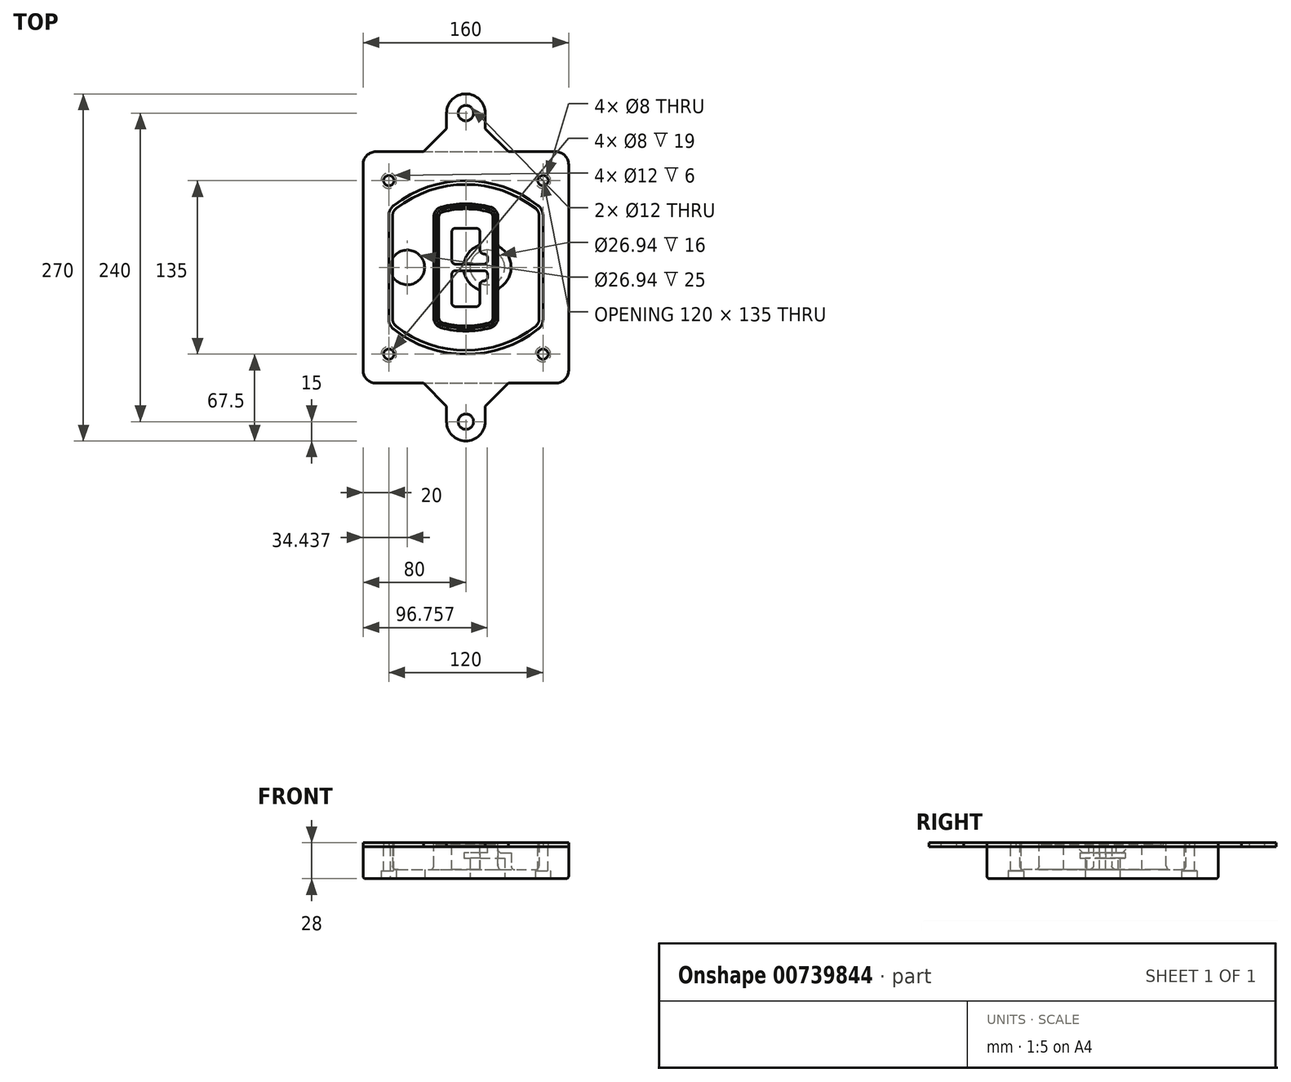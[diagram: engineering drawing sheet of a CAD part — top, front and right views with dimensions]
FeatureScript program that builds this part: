
annotation { "Feature Type Name" : "Feature", "Feature Type Description" : "" }
export const myFeature = defineFeature(function(context is Context, id is Id, definition is map)
    precondition{}
    {
        {
            var Q0;
            Q0=qCreatedBy(makeId("Top.planeOp"),FACE);
            var sketch = newSketch(context, id + "F0", { "sketchPlane" : qUnion([Q0])});
            skPoint(sketch, "E0.rect.middle", {"position": v(0, 0) * mm});
            skLineSegment(sketch, "E1.bottom", {"start": v(-70, -90) * mm, "end": v(70, -90) * mm});
            skLineSegment(sketch, "E1.top", {"start": v(-70, 90) * mm, "end": v(70, 90) * mm});
            skLineSegment(sketch, "E1.left", {"start": v(-80, -80) * mm, "end": v(-80, 80) * mm});
            skLineSegment(sketch, "E1.right", {"start": v(80, -80) * mm, "end": v(80, 80) * mm});
            skLineSegment(sketch, "E2", {"start": v(-80, 90) * mm, "end": v(80, -90) * mm, "construction": true});
            skLineSegment(sketch, "E3", {"start": v(80, 90) * mm, "end": v(-80, -90) * mm, "construction": true});
            skCircle(sketch, "E4", {"center": v(-60, 67.5) * mm, "radius": 4 * mm});
            skCircle(sketch, "E5", {"center": v(60, 67.5) * mm, "radius": 4 * mm});
            skCircle(sketch, "E6", {"center": v(60, -67.5) * mm, "radius": 4 * mm});
            skCircle(sketch, "E7", {"center": v(-60, -67.5) * mm, "radius": 4 * mm});
            skLineSegment(sketch, "E8", {"start": v(-60, 67.5) * mm, "end": v(60, 67.5) * mm, "construction": true});
            skLineSegment(sketch, "E9", {"start": v(60, 67.5) * mm, "end": v(60, -67.5) * mm, "construction": true});
            skLineSegment(sketch, "E10", {"start": v(60, -67.5) * mm, "end": v(-60, -67.5) * mm, "construction": true});
            skLineSegment(sketch, "E11", {"start": v(-60, -67.5) * mm, "end": v(-60, 67.5) * mm, "construction": true});
            skLineSegment(sketch, "E12", {"start": v(-60, 40.3) * mm, "end": v(-60, -40.3) * mm});
            skLineSegment(sketch, "E13", {"start": v(60, 40.3) * mm, "end": v(60, -40.3) * mm});
            skArc(sketch, "E14", {"start": v(56.15, 48.18) * mm, "mid": v(0, 67.5) * mm, "end": v(-56.15, 48.18) * mm});
            skArc(sketch, "E15", {"start": v(-56.15, -48.18) * mm, "mid": v(0, -67.5) * mm, "end": v(56.15, -48.18) * mm});
            skLineSegment(sketch, "E16", {"start": v(-60, 0) * mm, "end": v(60, 0) * mm, "construction": true});
            skPoint(sketch, "E17.visualSharp", {"position": v(-60, -45) * mm});
            skArc(sketch, "E17.filletArc", {"start": v(-60, -40.3) * mm, "mid": v(-58.99, -44.68) * mm, "end": v(-56.15, -48.18) * mm});
            skPoint(sketch, "E18.visualSharp", {"position": v(-60, 45) * mm});
            skArc(sketch, "E18.filletArc", {"start": v(-56.15, 48.18) * mm, "mid": v(-58.99, 44.68) * mm, "end": v(-60, 40.3) * mm});
            skPoint(sketch, "E19.visualSharp", {"position": v(60, 45) * mm});
            skArc(sketch, "E19.filletArc", {"start": v(60, 40.3) * mm, "mid": v(58.99, 44.68) * mm, "end": v(56.15, 48.18) * mm});
            skPoint(sketch, "E20.visualSharp", {"position": v(60, -45) * mm});
            skArc(sketch, "E20.filletArc", {"start": v(56.15, -48.18) * mm, "mid": v(58.99, -44.68) * mm, "end": v(60, -40.3) * mm});
            skPoint(sketch, "E21.visualSharp", {"position": v(-80, 90) * mm});
            skArc(sketch, "E21.filletArc", {"start": v(-70, 90) * mm, "mid": v(-77.07, 87.07) * mm, "end": v(-80, 80) * mm});
            skPoint(sketch, "E22.visualSharp", {"position": v(80, 90) * mm});
            skArc(sketch, "E22.filletArc", {"start": v(80, 80) * mm, "mid": v(77.07, 87.07) * mm, "end": v(70, 90) * mm});
            skPoint(sketch, "E23.visualSharp", {"position": v(80, -90) * mm});
            skArc(sketch, "E23.filletArc", {"start": v(70, -90) * mm, "mid": v(77.07, -87.07) * mm, "end": v(80, -80) * mm});
            skPoint(sketch, "E24.visualSharp", {"position": v(-80, -90) * mm});
            skArc(sketch, "E24.filletArc", {"start": v(-80, -80) * mm, "mid": v(-77.07, -87.07) * mm, "end": v(-70, -90) * mm});
            skArc(sketch, "E25.0", {"start": v(57, 40.3) * mm, "mid": v(56.3, 43.36) * mm, "end": v(54.3, 45.81) * mm});
            skLineSegment(sketch, "E25.1", {"start": v(57, 40.3) * mm, "end": v(57, -40.3) * mm});
            skArc(sketch, "E25.2", {"start": v(54.3, -45.81) * mm, "mid": v(56.3, -43.36) * mm, "end": v(57, -40.3) * mm});
            skArc(sketch, "E25.3", {"start": v(-54.3, -45.81) * mm, "mid": v(0, -64.5) * mm, "end": v(54.3, -45.81) * mm});
            skArc(sketch, "E25.4", {"start": v(-57, -40.3) * mm, "mid": v(-56.3, -43.36) * mm, "end": v(-54.3, -45.81) * mm});
            skArc(sketch, "E25.5", {"start": v(54.3, 45.81) * mm, "mid": v(0, 64.5) * mm, "end": v(-54.3, 45.81) * mm});
            skLineSegment(sketch, "E25.6", {"start": v(-57, 40.3) * mm, "end": v(-57, -40.3) * mm});
            skArc(sketch, "E25.7", {"start": v(-54.3, 45.81) * mm, "mid": v(-56.3, 43.36) * mm, "end": v(-57, 40.3) * mm});
            skArc(sketch, "E26.0", {"start": v(-58.62, 51.33) * mm, "mid": v(-62.58, 46.43) * mm, "end": v(-64, 40.3) * mm});
            skArc(sketch, "E26.1", {"start": v(58.62, 51.33) * mm, "mid": v(0, 71.5) * mm, "end": v(-58.62, 51.33) * mm});
            skArc(sketch, "E26.2", {"start": v(64, 40.3) * mm, "mid": v(62.58, 46.43) * mm, "end": v(58.62, 51.33) * mm});
            skLineSegment(sketch, "E26.3", {"start": v(64, 40.3) * mm, "end": v(64, -40.3) * mm});
            skArc(sketch, "E26.4", {"start": v(58.62, -51.33) * mm, "mid": v(62.58, -46.43) * mm, "end": v(64, -40.3) * mm});
            skLineSegment(sketch, "E26.5", {"start": v(-64, 40.3) * mm, "end": v(-64, -40.3) * mm});
            skArc(sketch, "E26.6", {"start": v(-58.62, -51.33) * mm, "mid": v(0, -71.5) * mm, "end": v(58.62, -51.33) * mm});
            skArc(sketch, "E26.7", {"start": v(-64, -40.3) * mm, "mid": v(-62.58, -46.43) * mm, "end": v(-58.62, -51.33) * mm});
            skSolve(sketch);
        }
        {
            var Q0;
            Q0=makeQuery(id+"F0.imprint","IMPRINT",FACE,{"disambiguationData":[TD([[makeQuery(id+"F0.imprint","IMPRINT",EDGE,{"derivedFrom":sQuery(id+"F0.wireOp",EDGE,"E1.bottom")}),1.0]])]});
            var Q1;
            Q1=makeQuery(id+"F0.imprint","IMPRINT",FACE,{"disambiguationData":[TD([[makeQuery(id+"F0.imprint","IMPRINT",EDGE,{"derivedFrom":sQuery(id+"F0.wireOp",EDGE,"E12")}),1.0]])]});
            var Q2;
            Q2=makeQuery(id+"F0.imprint","IMPRINT",FACE,{"disambiguationData":[TD([[makeQuery(id+"F0.imprint","IMPRINT",EDGE,{"derivedFrom":sQuery(id+"F0.wireOp",EDGE,"E25.0")}),1.0]])]});
            var Q3;
            Q3=makeQuery(id+"F0.imprint","IMPRINT",FACE,{"disambiguationData":[TD([[makeQuery(id+"F0.imprint","IMPRINT",EDGE,{"derivedFrom":sQuery(id+"F0.wireOp",EDGE,"E12")}),-1.0]])]});
            extrude(context, id + "F1", {"entities" : qUnion([Q0, Q1, Q2, Q3]), "oppositeDirection" : true, "depth" : 25 * mm});
        }
        {
            var Q0;
            Q0=makeQuery(id+"F0.imprint","IMPRINT",FACE,{"disambiguationData":[TD([[makeQuery(id+"F0.imprint","IMPRINT",EDGE,{"derivedFrom":sQuery(id+"F0.wireOp",EDGE,"E12")}),1.0]])]});
            extrude(context, id + "F2", {"entities" : qUnion([Q0]), "operationType" : NewBodyOperationType.ADD, "depth" : 3 * mm});
        }
        {
            var Q0;
            Q0=makeQuery(id+"F0.imprint","IMPRINT",FACE,{"disambiguationData":[TD([[makeQuery(id+"F0.imprint","IMPRINT",EDGE,{"derivedFrom":sQuery(id+"F0.wireOp",EDGE,"E25.0")}),1.0]])]});
            extrude(context, id + "F3", {"entities" : qUnion([Q0]), "operationType" : NewBodyOperationType.REMOVE, "oppositeDirection" : true, "depth" : 18 * mm});
        }
        {
            var Q0;
            Q0=makeQuery(id+"F2.opExtrude","CAP_FACE",FACE,{"disambiguationData":[OSD([sQuery(id+"F0.wireOp",EDGE,"E12"),sQuery(id+"F0.wireOp",EDGE,"E13"),sQuery(id+"F0.wireOp",EDGE,"E14"),sQuery(id+"F0.wireOp",EDGE,"E15"),sQuery(id+"F0.wireOp",EDGE,"E17.filletArc"),sQuery(id+"F0.wireOp",EDGE,"E18.filletArc"),sQuery(id+"F0.wireOp",EDGE,"E19.filletArc"),sQuery(id+"F0.wireOp",EDGE,"E20.filletArc"),sQuery(id+"F0.wireOp",EDGE,"E25.0"),sQuery(id+"F0.wireOp",EDGE,"E25.1"),sQuery(id+"F0.wireOp",EDGE,"E25.2"),sQuery(id+"F0.wireOp",EDGE,"E25.3"),sQuery(id+"F0.wireOp",EDGE,"E25.4"),sQuery(id+"F0.wireOp",EDGE,"E25.5"),sQuery(id+"F0.wireOp",EDGE,"E25.6"),sQuery(id+"F0.wireOp",EDGE,"E25.7")])],"isStart":false});
            var sketch = newSketch(context, id + "F4", { "sketchPlane" : qUnion([Q0])});
            skArc(sketch, "E27.0", {"start": v(-19.08, -46.97) * mm, "mid": v(0, -49.5) * mm, "end": v(19.08, -46.97) * mm});
            skArc(sketch, "E28.0", {"start": v(19.08, 46.97) * mm, "mid": v(0, 49.5) * mm, "end": v(-19.08, 46.97) * mm});
            skLineSegment(sketch, "E29", {"start": v(-25, 39.25) * mm, "end": v(-25, -39.25) * mm});
            skLineSegment(sketch, "E30", {"start": v(25, 39.25) * mm, "end": v(25, -39.25) * mm});
            skLineSegment(sketch, "E31", {"start": v(-25, 45.1) * mm, "end": v(25, 45.1) * mm, "construction": true});
            skLineSegment(sketch, "E32", {"start": v(-25, -45.1) * mm, "end": v(25, -45.1) * mm, "construction": true});
            skPoint(sketch, "E33.visualSharp", {"position": v(-25, 45.1) * mm});
            skArc(sketch, "E33.filletArc", {"start": v(-19.08, 46.97) * mm, "mid": v(-23.35, 44.11) * mm, "end": v(-25, 39.25) * mm});
            skPoint(sketch, "E34.visualSharp", {"position": v(25, 45.1) * mm});
            skArc(sketch, "E34.filletArc", {"start": v(25, 39.25) * mm, "mid": v(23.35, 44.11) * mm, "end": v(19.08, 46.97) * mm});
            skPoint(sketch, "E35.visualSharp", {"position": v(25, -45.1) * mm});
            skArc(sketch, "E35.filletArc", {"start": v(19.08, -46.97) * mm, "mid": v(23.35, -44.11) * mm, "end": v(25, -39.25) * mm});
            skPoint(sketch, "E36.visualSharp", {"position": v(-25, -45.1) * mm});
            skArc(sketch, "E36.filletArc", {"start": v(-25, -39.25) * mm, "mid": v(-23.35, -44.11) * mm, "end": v(-19.08, -46.97) * mm});
            skArc(sketch, "E37.0", {"start": v(54.3, 45.81) * mm, "mid": v(0, 64.5) * mm, "end": v(-54.3, 45.81) * mm});
            skArc(sketch, "E37.1", {"start": v(-54.3, 45.81) * mm, "mid": v(-56.3, 43.36) * mm, "end": v(-57, 40.3) * mm});
            skLineSegment(sketch, "E37.2", {"start": v(-57, 40.3) * mm, "end": v(-57, -40.3) * mm});
            skArc(sketch, "E37.3", {"start": v(-57, -40.3) * mm, "mid": v(-56.3, -43.36) * mm, "end": v(-54.3, -45.81) * mm});
            skArc(sketch, "E37.4", {"start": v(-54.3, -45.81) * mm, "mid": v(0, -64.5) * mm, "end": v(54.3, -45.81) * mm});
            skArc(sketch, "E37.5", {"start": v(54.3, -45.81) * mm, "mid": v(56.3, -43.36) * mm, "end": v(57, -40.3) * mm});
            skLineSegment(sketch, "E37.6", {"start": v(57, 40.3) * mm, "end": v(57, -40.3) * mm});
            skArc(sketch, "E37.7", {"start": v(57, 40.3) * mm, "mid": v(56.3, 43.36) * mm, "end": v(54.3, 45.81) * mm});
            skLineSegment(sketch, "E38.0", {"start": v(23, 39.25) * mm, "end": v(23, -39.25) * mm});
            skArc(sketch, "E38.1", {"start": v(18.56, -45.04) * mm, "mid": v(21.76, -42.9) * mm, "end": v(23, -39.25) * mm});
            skArc(sketch, "E38.2", {"start": v(-18.56, -45.04) * mm, "mid": v(0, -47.5) * mm, "end": v(18.56, -45.04) * mm});
            skArc(sketch, "E38.3", {"start": v(-23, -39.25) * mm, "mid": v(-21.76, -42.9) * mm, "end": v(-18.56, -45.04) * mm});
            skLineSegment(sketch, "E38.4", {"start": v(-23, 39.25) * mm, "end": v(-23, -39.25) * mm});
            skArc(sketch, "E38.5", {"start": v(23, 39.25) * mm, "mid": v(21.76, 42.9) * mm, "end": v(18.56, 45.04) * mm});
            skArc(sketch, "E38.6", {"start": v(-18.56, 45.04) * mm, "mid": v(-21.76, 42.9) * mm, "end": v(-23, 39.25) * mm});
            skArc(sketch, "E38.7", {"start": v(18.56, 45.04) * mm, "mid": v(0, 47.5) * mm, "end": v(-18.56, 45.04) * mm});
            skArc(sketch, "E39.0", {"start": v(21, 39.25) * mm, "mid": v(20.18, 41.68) * mm, "end": v(18.04, 43.1) * mm});
            skLineSegment(sketch, "E39.1", {"start": v(21, 39.25) * mm, "end": v(21, -39.25) * mm});
            skArc(sketch, "E39.2", {"start": v(18.04, -43.1) * mm, "mid": v(20.18, -41.68) * mm, "end": v(21, -39.25) * mm});
            skArc(sketch, "E39.3", {"start": v(-18.04, -43.1) * mm, "mid": v(0, -45.5) * mm, "end": v(18.04, -43.1) * mm});
            skArc(sketch, "E39.4", {"start": v(-21, -39.25) * mm, "mid": v(-20.18, -41.68) * mm, "end": v(-18.04, -43.1) * mm});
            skArc(sketch, "E39.5", {"start": v(18.04, 43.1) * mm, "mid": v(0, 45.5) * mm, "end": v(-18.04, 43.1) * mm});
            skLineSegment(sketch, "E39.6", {"start": v(-21, 39.25) * mm, "end": v(-21, -39.25) * mm});
            skArc(sketch, "E39.7", {"start": v(-18.04, 43.1) * mm, "mid": v(-20.18, 41.68) * mm, "end": v(-21, 39.25) * mm});
            skLineSegment(sketch, "E40", {"start": v(-25, 0) * mm, "end": v(25, 0) * mm, "construction": true});
            skLineSegment(sketch, "E41", {"start": v(-11, 5.5) * mm, "end": v(-11, 27.5) * mm});
            skLineSegment(sketch, "E42", {"start": v(-8, 30.5) * mm, "end": v(8, 30.5) * mm});
            skLineSegment(sketch, "E43", {"start": v(11, 27.5) * mm, "end": v(11, 13.5) * mm});
            skLineSegment(sketch, "E44", {"start": v(14, 10.5) * mm, "end": v(14, 10.5) * mm});
            skLineSegment(sketch, "E45", {"start": v(17, 7.5) * mm, "end": v(17, 5.5) * mm});
            skLineSegment(sketch, "E46", {"start": v(14, 2.5) * mm, "end": v(-8, 2.5) * mm});
            skPoint(sketch, "E47.visualSharp", {"position": v(-11, 30.5) * mm});
            skArc(sketch, "E47.filletArc", {"start": v(-8, 30.5) * mm, "mid": v(-10.12, 29.62) * mm, "end": v(-11, 27.5) * mm});
            skPoint(sketch, "E48.visualSharp", {"position": v(11, 30.5) * mm});
            skArc(sketch, "E48.filletArc", {"start": v(11, 27.5) * mm, "mid": v(10.12, 29.62) * mm, "end": v(8, 30.5) * mm});
            skPoint(sketch, "E49.visualSharp", {"position": v(11, 10.5) * mm});
            skArc(sketch, "E49.filletArc", {"start": v(11, 13.5) * mm, "mid": v(11.88, 11.38) * mm, "end": v(14, 10.5) * mm});
            skPoint(sketch, "E50.visualSharp", {"position": v(17, 10.5) * mm});
            skArc(sketch, "E50.filletArc", {"start": v(17, 7.5) * mm, "mid": v(16.12, 9.62) * mm, "end": v(14, 10.5) * mm});
            skPoint(sketch, "E51.visualSharp", {"position": v(17, 2.5) * mm});
            skArc(sketch, "E51.filletArc", {"start": v(14, 2.5) * mm, "mid": v(16.12, 3.38) * mm, "end": v(17, 5.5) * mm});
            skPoint(sketch, "E52.visualSharp", {"position": v(-11, 2.5) * mm});
            skArc(sketch, "E52.filletArc", {"start": v(-11, 5.5) * mm, "mid": v(-10.12, 3.38) * mm, "end": v(-8, 2.5) * mm});
            skLineSegment(sketch, "E53.0.MirrorCS", {"start": v(14, -2.5) * mm, "end": v(-8, -2.5) * mm});
            skArc(sketch, "E54.0.MirrorCS", {"start": v(-11, -5.5) * mm, "mid": v(-10.12, -3.38) * mm, "end": v(-8, -2.5) * mm});
            skLineSegment(sketch, "E55.0.MirrorCS", {"start": v(-11, -5.5) * mm, "end": v(-11, -27.5) * mm});
            skArc(sketch, "E56.0.MirrorCS", {"start": v(-8, -30.5) * mm, "mid": v(-10.12, -29.62) * mm, "end": v(-11, -27.5) * mm});
            skLineSegment(sketch, "E57.0.MirrorCS", {"start": v(-8, -30.5) * mm, "end": v(8, -30.5) * mm});
            skArc(sketch, "E58.0.MirrorCS", {"start": v(11, -27.5) * mm, "mid": v(10.12, -29.62) * mm, "end": v(8, -30.5) * mm});
            skLineSegment(sketch, "E59.0.MirrorCS", {"start": v(11, -27.5) * mm, "end": v(11, -13.5) * mm});
            skArc(sketch, "E60.0.MirrorCS", {"start": v(11, -13.5) * mm, "mid": v(11.88, -11.38) * mm, "end": v(14, -10.5) * mm});
            skArc(sketch, "E61.0.MirrorCS", {"start": v(17, -7.5) * mm, "mid": v(16.12, -9.62) * mm, "end": v(14, -10.5) * mm});
            skLineSegment(sketch, "E62.0.MirrorCS", {"start": v(17, -7.5) * mm, "end": v(17, -5.5) * mm});
            skArc(sketch, "E63.0.MirrorCS", {"start": v(14, -2.5) * mm, "mid": v(16.12, -3.38) * mm, "end": v(17, -5.5) * mm});
            skSolve(sketch);
        }
        {
            var Q0;
            Q0=makeQuery(id+"F4.imprint","IMPRINT",FACE,{"disambiguationData":[TD([[makeQuery(id+"F4.imprint","IMPRINT",EDGE,{"derivedFrom":sQuery(id+"F4.wireOp",EDGE,"E27.0")}),1.0]])]});
            var Q1;
            Q1=makeQuery(id+"F4.imprint","IMPRINT",FACE,{"disambiguationData":[TD([[makeQuery(id+"F4.imprint","IMPRINT",EDGE,{"derivedFrom":sQuery(id+"F4.wireOp",EDGE,"E38.0")}),-1.0]])]});
            var Q2;
            Q2=makeQuery(id+"F4.imprint","IMPRINT",FACE,{"disambiguationData":[TD([[makeQuery(id+"F4.imprint","IMPRINT",EDGE,{"derivedFrom":sQuery(id+"F4.wireOp",EDGE,"E39.0")}),1.0]])]});
            extrude(context, id + "F5", {"entities" : qUnion([Q0, Q1, Q2]), "operationType" : NewBodyOperationType.ADD, "endBound" : BoundingType.UP_TO_NEXT, "oppositeDirection" : true, "depth" : 25 * mm});
        }
        {
            var Q0;
            Q0=makeQuery(id+"F4.imprint","IMPRINT",FACE,{"disambiguationData":[TD([[makeQuery(id+"F4.imprint","IMPRINT",EDGE,{"derivedFrom":sQuery(id+"F4.wireOp",EDGE,"E38.0")}),-1.0]])]});
            extrude(context, id + "F6", {"entities" : qUnion([Q0]), "operationType" : NewBodyOperationType.REMOVE, "oppositeDirection" : true, "depth" : 2 * mm});
        }
        {
            var Q0;
            Q0=makeQuery(id+"F1.opExtrude","CAP_FACE",FACE,{"disambiguationData":[OSD([sQuery(id+"F0.wireOp",EDGE,"E1.bottom"),sQuery(id+"F0.wireOp",EDGE,"E1.top"),sQuery(id+"F0.wireOp",EDGE,"E1.left"),sQuery(id+"F0.wireOp",EDGE,"E1.right"),sQuery(id+"F0.wireOp",EDGE,"E4"),sQuery(id+"F0.wireOp",EDGE,"E5"),sQuery(id+"F0.wireOp",EDGE,"E6"),sQuery(id+"F0.wireOp",EDGE,"E7"),sQuery(id+"F0.wireOp",EDGE,"E21.filletArc"),sQuery(id+"F0.wireOp",EDGE,"E22.filletArc"),sQuery(id+"F0.wireOp",EDGE,"E23.filletArc"),sQuery(id+"F0.wireOp",EDGE,"E24.filletArc")])],"isStart":false});
            var sketch = newSketch(context, id + "F7", { "sketchPlane" : qUnion([Q0])});
            skCircle(sketch, "E64", {"center": v(16.76, 0) * mm, "radius": 13.47 * mm});
            skCircle(sketch, "E65", {"center": v(-45.56, 0) * mm, "radius": 13.47 * mm});
            skLineSegment(sketch, "E66", {"start": v(80, 0) * mm, "end": v(-80, 0) * mm});
            skCircle(sketch, "E67", {"center": v(16.76, 0) * mm, "radius": 18.47 * mm});
            skCircle(sketch, "E68", {"center": v(60, -67.5) * mm, "radius": 6 * mm});
            skCircle(sketch, "E69", {"center": v(-60, -67.5) * mm, "radius": 6 * mm});
            skCircle(sketch, "E70", {"center": v(-60, 67.5) * mm, "radius": 6 * mm});
            skCircle(sketch, "E71", {"center": v(60, 67.5) * mm, "radius": 6 * mm});
            skSolve(sketch);
        }
        {
            var Q0;
            {var subQ1=sQuery(id+"F7.wireOp",EDGE,"E66");var subQ4=sQuery(id+"F7.wireOp",EDGE,"E64");var subQ6=makeQuery(id+"F7.imprint","INTERSECT",VERTEX,{"disambiguationData":[OD(0.0)],"derivedFrom":[subQ4,subQ1]});Q0=makeQuery(id+"F7.imprint","IMPRINT",FACE,{"disambiguationData":[TD([[makeQuery(id+"F7.imprint","IMPRINT",EDGE,{"disambiguationData":[TD([[subQ6,-1.0]])],"derivedFrom":subQ4}),-1.0]])]});}
            var Q1;
            {var subQ0=sQuery(id+"F7.wireOp",EDGE,"E66");var subQ1=sQuery(id+"F7.wireOp",EDGE,"E64");var subQ3=makeQuery(id+"F7.imprint","INTERSECT",VERTEX,{"disambiguationData":[OD(0.0)],"derivedFrom":[subQ1,subQ0]});Q1=makeQuery(id+"F7.imprint","IMPRINT",FACE,{"disambiguationData":[TD([[makeQuery(id+"F7.imprint","IMPRINT",EDGE,{"disambiguationData":[TD([[subQ3,-1.0]])],"derivedFrom":subQ1}),1.0]])]});}
            var Q2;
            {var subQ0=sQuery(id+"F7.wireOp",EDGE,"E66");var subQ1=sQuery(id+"F7.wireOp",EDGE,"E64");var subQ3=makeQuery(id+"F7.imprint","INTERSECT",VERTEX,{"disambiguationData":[OD(0.0)],"derivedFrom":[subQ1,subQ0]});Q2=makeQuery(id+"F7.imprint","IMPRINT",FACE,{"disambiguationData":[TD([[makeQuery(id+"F7.imprint","IMPRINT",EDGE,{"disambiguationData":[TD([[subQ3,1.0]])],"derivedFrom":subQ1}),1.0]])]});}
            var Q3;
            {var subQ1=sQuery(id+"F7.wireOp",EDGE,"E66");var subQ4=sQuery(id+"F7.wireOp",EDGE,"E64");var subQ6=makeQuery(id+"F7.imprint","INTERSECT",VERTEX,{"disambiguationData":[OD(0.0)],"derivedFrom":[subQ4,subQ1]});Q3=makeQuery(id+"F7.imprint","IMPRINT",FACE,{"disambiguationData":[TD([[makeQuery(id+"F7.imprint","IMPRINT",EDGE,{"disambiguationData":[TD([[subQ6,1.0]])],"derivedFrom":subQ4}),-1.0]])]});}
            extrude(context, id + "F8", {"entities" : qUnion([Q0, Q1, Q2, Q3]), "operationType" : NewBodyOperationType.ADD, "oppositeDirection" : true, "depth" : 20 * mm});
        }
        {
            var Q0;
            {var subQ0=sQuery(id+"F7.wireOp",EDGE,"E66");var subQ1=sQuery(id+"F7.wireOp",EDGE,"E64");var subQ3=makeQuery(id+"F7.imprint","INTERSECT",VERTEX,{"disambiguationData":[OD(0.0)],"derivedFrom":[subQ1,subQ0]});Q0=makeQuery(id+"F7.imprint","IMPRINT",FACE,{"disambiguationData":[TD([[makeQuery(id+"F7.imprint","IMPRINT",EDGE,{"disambiguationData":[TD([[subQ3,-1.0]])],"derivedFrom":subQ1}),1.0]])]});}
            var Q1;
            {var subQ0=sQuery(id+"F7.wireOp",EDGE,"E66");var subQ1=sQuery(id+"F7.wireOp",EDGE,"E64");var subQ3=makeQuery(id+"F7.imprint","INTERSECT",VERTEX,{"disambiguationData":[OD(0.0)],"derivedFrom":[subQ1,subQ0]});Q1=makeQuery(id+"F7.imprint","IMPRINT",FACE,{"disambiguationData":[TD([[makeQuery(id+"F7.imprint","IMPRINT",EDGE,{"disambiguationData":[TD([[subQ3,1.0]])],"derivedFrom":subQ1}),1.0]])]});}
            extrude(context, id + "F9", {"entities" : qUnion([Q0, Q1]), "operationType" : NewBodyOperationType.REMOVE, "oppositeDirection" : true, "depth" : 16 * mm});
        }
        {
            var Q0;
            {var subQ0=sQuery(id+"F7.wireOp",EDGE,"E66");var subQ1=sQuery(id+"F7.wireOp",EDGE,"E65");var subQ3=makeQuery(id+"F7.imprint","INTERSECT",VERTEX,{"disambiguationData":[OD(0.0)],"derivedFrom":[subQ1,subQ0]});Q0=makeQuery(id+"F7.imprint","IMPRINT",FACE,{"disambiguationData":[TD([[makeQuery(id+"F7.imprint","IMPRINT",EDGE,{"disambiguationData":[TD([[subQ3,-1.0]])],"derivedFrom":subQ1}),1.0]])]});}
            var Q1;
            {var subQ0=sQuery(id+"F7.wireOp",EDGE,"E66");var subQ1=sQuery(id+"F7.wireOp",EDGE,"E65");var subQ3=makeQuery(id+"F7.imprint","INTERSECT",VERTEX,{"disambiguationData":[OD(0.0)],"derivedFrom":[subQ1,subQ0]});Q1=makeQuery(id+"F7.imprint","IMPRINT",FACE,{"disambiguationData":[TD([[makeQuery(id+"F7.imprint","IMPRINT",EDGE,{"disambiguationData":[TD([[subQ3,1.0]])],"derivedFrom":subQ1}),1.0]])]});}
            extrude(context, id + "F10", {"entities" : qUnion([Q0, Q1]), "operationType" : NewBodyOperationType.REMOVE, "oppositeDirection" : true, "depth" : 25 * mm});
        }
        {
            var Q0;
            Q0=makeQuery(id+"F7.imprint","IMPRINT",FACE,{"disambiguationData":[TD([[makeQuery(id+"F7.imprint","IMPRINT",EDGE,{"derivedFrom":sQuery(id+"F7.wireOp",EDGE,"E68")}),1.0]])]});
            var Q1;
            Q1=makeQuery(id+"F7.imprint","IMPRINT",FACE,{"disambiguationData":[TD([[makeQuery(id+"F7.imprint","IMPRINT",EDGE,{"derivedFrom":makeQuery(id+"F1.opExtrude","CAP_EDGE",EDGE,{"disambiguationData":[OSD([sQuery(id+"F0.wireOp",EDGE,"E5")])],"isStart":false})}),-1.0]])]});
            var Q2;
            Q2=makeQuery(id+"F7.imprint","IMPRINT",FACE,{"disambiguationData":[TD([[makeQuery(id+"F7.imprint","IMPRINT",EDGE,{"derivedFrom":sQuery(id+"F7.wireOp",EDGE,"E69")}),1.0]])]});
            var Q3;
            Q3=makeQuery(id+"F7.imprint","IMPRINT",FACE,{"disambiguationData":[TD([[makeQuery(id+"F7.imprint","IMPRINT",EDGE,{"derivedFrom":makeQuery(id+"F1.opExtrude","CAP_EDGE",EDGE,{"disambiguationData":[OSD([sQuery(id+"F0.wireOp",EDGE,"E4")])],"isStart":false})}),-1.0]])]});
            var Q4;
            Q4=makeQuery(id+"F7.imprint","IMPRINT",FACE,{"disambiguationData":[TD([[makeQuery(id+"F7.imprint","IMPRINT",EDGE,{"derivedFrom":sQuery(id+"F7.wireOp",EDGE,"E70")}),1.0]])]});
            var Q5;
            Q5=makeQuery(id+"F7.imprint","IMPRINT",FACE,{"disambiguationData":[TD([[makeQuery(id+"F7.imprint","IMPRINT",EDGE,{"derivedFrom":makeQuery(id+"F1.opExtrude","CAP_EDGE",EDGE,{"disambiguationData":[OSD([sQuery(id+"F0.wireOp",EDGE,"E7")])],"isStart":false})}),-1.0]])]});
            var Q6;
            Q6=makeQuery(id+"F7.imprint","IMPRINT",FACE,{"disambiguationData":[TD([[makeQuery(id+"F7.imprint","IMPRINT",EDGE,{"derivedFrom":sQuery(id+"F7.wireOp",EDGE,"E71")}),1.0]])]});
            var Q7;
            Q7=makeQuery(id+"F7.imprint","IMPRINT",FACE,{"disambiguationData":[TD([[makeQuery(id+"F7.imprint","IMPRINT",EDGE,{"derivedFrom":makeQuery(id+"F1.opExtrude","CAP_EDGE",EDGE,{"disambiguationData":[OSD([sQuery(id+"F0.wireOp",EDGE,"E6")])],"isStart":false})}),-1.0]])]});
            extrude(context, id + "F11", {"entities" : qUnion([Q0, Q1, Q2, Q3, Q4, Q5, Q6, Q7]), "operationType" : NewBodyOperationType.REMOVE, "oppositeDirection" : true, "depth" : 6 * mm});
        }
        {
            var Q0;
            Q0=makeQuery(id+"F9.boolean.opBoolean","COPY",FACE,{"derivedFrom":makeQuery(id+"F9.opExtrude","CAP_FACE",FACE,{"disambiguationData":[OSD([sQuery(id+"F7.wireOp",EDGE,"E64")])],"isStart":false})});
            var sketch = newSketch(context, id + "F12", { "sketchPlane" : qUnion([Q0])});
            skArc(sketch, "E72.0", {"start": v(11, 17.55) * mm, "mid": v(2.57, 11.82) * mm, "end": v(-1.54, 2.5) * mm});
            skArc(sketch, "E72.1", {"start": v(-1.54, -2.5) * mm, "mid": v(2.57, -11.82) * mm, "end": v(11, -17.55) * mm});
            skLineSegment(sketch, "E73", {"start": v(-1.54, -2.5) * mm, "end": v(14, -2.5) * mm});
            skLineSegment(sketch, "E74.0", {"start": v(14, 2.5) * mm, "end": v(-1.54, 2.5) * mm});
            skArc(sketch, "E74.1", {"start": v(14, 2.5) * mm, "mid": v(16.12, 3.38) * mm, "end": v(17, 5.5) * mm});
            skLineSegment(sketch, "E74.2", {"start": v(17, 7.5) * mm, "end": v(17, 5.5) * mm});
            skArc(sketch, "E74.3", {"start": v(17, 7.5) * mm, "mid": v(16.12, 9.62) * mm, "end": v(14, 10.5) * mm});
            skArc(sketch, "E74.4", {"start": v(11, 13.5) * mm, "mid": v(11.88, 11.38) * mm, "end": v(14, 10.5) * mm});
            skLineSegment(sketch, "E74.5", {"start": v(11, 17.55) * mm, "end": v(11, 13.5) * mm});
            skLineSegment(sketch, "E74.7", {"start": v(14, -2.5) * mm, "end": v(-1.54, -2.5) * mm});
            skArc(sketch, "E74.8", {"start": v(14, -2.5) * mm, "mid": v(16.12, -3.38) * mm, "end": v(17, -5.5) * mm});
            skLineSegment(sketch, "E74.9", {"start": v(17, -7.5) * mm, "end": v(17, -5.5) * mm});
            skArc(sketch, "E74.10", {"start": v(17, -7.5) * mm, "mid": v(16.12, -9.62) * mm, "end": v(14, -10.5) * mm});
            skArc(sketch, "E74.11", {"start": v(11, -13.5) * mm, "mid": v(11.88, -11.38) * mm, "end": v(14, -10.5) * mm});
            skLineSegment(sketch, "E74.12", {"start": v(11, -17.55) * mm, "end": v(11, -13.5) * mm});
            skPoint(sketch, "E75.orphan", {"position": v(11, -27.5) * mm});
            skPoint(sketch, "E76.orphan", {"position": v(-8, -2.5) * mm});
            skPoint(sketch, "E77.orphan", {"position": v(-8, 2.5) * mm});
            skPoint(sketch, "E78.orphan", {"position": v(11, 27.5) * mm});
            skSolve(sketch);
        }
        {
            var Q0;
            {var subQ7=sQuery(id+"F12.wireOp",EDGE,"E72.0");var subQ14=sQuery(id+"F12.wireOp",EDGE,"E72.1");var subQ16=sQuery(id+"F12.wireOp",EDGE,"E74.1");var subQ18=sQuery(id+"F12.wireOp",EDGE,"E74.8");Q0=qUnion([makeQuery(id+"F12.imprint","IMPRINT",FACE,{"disambiguationData":[TD([[makeQuery(id+"F12.imprint","IMPRINT",EDGE,{"derivedFrom":subQ7}),1.0]])]}),makeQuery(id+"F12.imprint","IMPRINT",FACE,{"disambiguationData":[TD([[makeQuery(id+"F12.imprint","IMPRINT",EDGE,{"derivedFrom":subQ14}),1.0]])]}),makeQuery(id+"F12.imprint","IMPRINT",FACE,{"disambiguationData":[TD([[makeQuery(id+"F12.imprint","IMPRINT",EDGE,{"derivedFrom":subQ16}),1.0]])]}),makeQuery(id+"F12.imprint","IMPRINT",FACE,{"disambiguationData":[TD([[makeQuery(id+"F12.imprint","IMPRINT",EDGE,{"derivedFrom":subQ18}),-1.0]])]})]);}
            var Q1;
            Q1=makeQuery(id+"F5.boolean.opBoolean","SPLIT",FACE,{"disambiguationData":[TD([makeQuery(id+"F5.opExtrude","SWEPT_FACE",FACE,{"disambiguationData":[OSD([sQuery(id+"F4.wireOp",EDGE,"E41")])]})])],"derivedFrom":makeQuery(id+"F3.boolean.opBoolean","COPY",FACE,{"derivedFrom":makeQuery(id+"F3.opExtrude","CAP_FACE",FACE,{"disambiguationData":[OSD([sQuery(id+"F0.wireOp",EDGE,"E25.0"),sQuery(id+"F0.wireOp",EDGE,"E25.1"),sQuery(id+"F0.wireOp",EDGE,"E25.2"),sQuery(id+"F0.wireOp",EDGE,"E25.3"),sQuery(id+"F0.wireOp",EDGE,"E25.4"),sQuery(id+"F0.wireOp",EDGE,"E25.5"),sQuery(id+"F0.wireOp",EDGE,"E25.6"),sQuery(id+"F0.wireOp",EDGE,"E25.7")])],"isStart":false})})});
            extrude(context, id + "F13", {"entities" : qUnion([Q0]), "operationType" : NewBodyOperationType.REMOVE, "endBound" : BoundingType.UP_TO_SURFACE, "endBoundEntityFace" : qUnion([Q1]), "depth" : 25 * mm});
        }
        {
            var Q0;
            Q0=makeQuery(id+"F3.boolean.opBoolean","COPY",EDGE,{"derivedFrom":makeQuery(id+"F3.opExtrude","CAP_EDGE",EDGE,{"disambiguationData":[OSD([sQuery(id+"F0.wireOp",EDGE,"E25.6")])],"isStart":false})});
            var Q1;
            Q1=makeQuery(id+"F8.boolean.opBoolean","INTERSECT",EDGE,{"derivedFrom":[makeQuery(id+"F5.opExtrude","SWEPT_FACE",FACE,{"disambiguationData":[OSD([sQuery(id+"F4.wireOp",EDGE,"E30")])]}),makeQuery(id+"F8.opExtrude","CAP_FACE",FACE,{"disambiguationData":[OSD([sQuery(id+"F7.wireOp",EDGE,"E67")])],"isStart":false})]});
            var Q2;
            Q2=makeQuery(id+"F8.boolean.opBoolean","INTERSECT",EDGE,{"disambiguationData":[OD(1.0)],"derivedFrom":[makeQuery(id+"F5.opExtrude","SWEPT_FACE",FACE,{"disambiguationData":[OSD([sQuery(id+"F4.wireOp",EDGE,"E30")])]}),makeQuery(id+"F8.opExtrude","SWEPT_FACE",FACE,{"disambiguationData":[OSD([sQuery(id+"F7.wireOp",EDGE,"E67")])]})]});
            var Q3;
            {var subQ0=sQuery(id+"F4.wireOp",EDGE,"E30");Q3=makeQuery(id+"F8.boolean.opBoolean","SPLIT",EDGE,{"disambiguationData":[TD([makeQuery(id+"F5.opExtrude","SWEPT_FACE",FACE,{"disambiguationData":[OSD([sQuery(id+"F4.wireOp",EDGE,"E35.filletArc")])]})])],"derivedFrom":makeQuery(id+"F5.opExtrude","CAP_EDGE",EDGE,{"disambiguationData":[OSD([subQ0])],"isStart":false})});}
            var Q4;
            {var subQ0=sQuery(id+"F0.wireOp",EDGE,"E25.7");var subQ1=sQuery(id+"F0.wireOp",EDGE,"E25.1");var subQ2=sQuery(id+"F0.wireOp",EDGE,"E25.6");var subQ3=sQuery(id+"F0.wireOp",EDGE,"E25.5");var subQ4=sQuery(id+"F0.wireOp",EDGE,"E25.4");var subQ5=sQuery(id+"F0.wireOp",EDGE,"E25.0");var subQ6=sQuery(id+"F0.wireOp",EDGE,"E25.2");var subQ7=sQuery(id+"F0.wireOp",EDGE,"E25.3");Q4=makeQuery(id+"F8.boolean.opBoolean","INTERSECT",EDGE,{"derivedFrom":[makeQuery(id+"F5.boolean.opBoolean","SPLIT",FACE,{"disambiguationData":[TD([makeQuery(id+"F2.opExtrude","SWEPT_FACE",FACE,{"disambiguationData":[OSD([subQ5])]})])],"derivedFrom":makeQuery(id+"F3.boolean.opBoolean","COPY",FACE,{"derivedFrom":makeQuery(id+"F3.opExtrude","CAP_FACE",FACE,{"disambiguationData":[OSD([subQ5,subQ1,subQ6,subQ7,subQ4,subQ3,subQ2,subQ0])],"isStart":false})})}),makeQuery(id+"F8.opExtrude","SWEPT_FACE",FACE,{"disambiguationData":[OSD([sQuery(id+"F7.wireOp",EDGE,"E67")])]})]});}
            var Q5;
            Q5=makeQuery(id+"F8.boolean.opBoolean","INTERSECT",EDGE,{"disambiguationData":[OD(0.0)],"derivedFrom":[makeQuery(id+"F5.opExtrude","SWEPT_FACE",FACE,{"disambiguationData":[OSD([sQuery(id+"F4.wireOp",EDGE,"E30")])]}),makeQuery(id+"F8.opExtrude","SWEPT_FACE",FACE,{"disambiguationData":[OSD([sQuery(id+"F7.wireOp",EDGE,"E67")])]})]});
            fillet(context, id + "F14", {"entities" : qUnion([Q0, Q1, Q2, Q3, Q4, Q5]), "radius" : 3 * mm, "tangentPropagation" : true, "allowEdgeOverflow" : false});
        }
        {
            var Q0;
            Q0=makeQuery(id+"F1.opExtrude","CAP_EDGE",EDGE,{"disambiguationData":[OSD([sQuery(id+"F0.wireOp",EDGE,"E1.bottom")])],"isStart":false});
            fillet(context, id + "F15", {"entities" : qUnion([Q0]), "radius" : 2 * mm, "tangentPropagation" : true, "allowEdgeOverflow" : false});
        }
        {
            var Q0;
            {var subQ0=sQuery(id+"F0.wireOp",EDGE,"E21.filletArc");var subQ1=sQuery(id+"F0.wireOp",EDGE,"E7");var subQ2=sQuery(id+"F0.wireOp",EDGE,"E6");var subQ3=sQuery(id+"F0.wireOp",EDGE,"E5");var subQ4=sQuery(id+"F0.wireOp",EDGE,"E4");var subQ5=sQuery(id+"F0.wireOp",EDGE,"E22.filletArc");var subQ6=sQuery(id+"F0.wireOp",EDGE,"E1.bottom");var subQ7=sQuery(id+"F0.wireOp",EDGE,"E1.right");var subQ8=sQuery(id+"F0.wireOp",EDGE,"E1.top");var subQ9=sQuery(id+"F0.wireOp",EDGE,"E1.left");var subQ10=sQuery(id+"F0.wireOp",EDGE,"E23.filletArc");var subQ11=sQuery(id+"F0.wireOp",EDGE,"E24.filletArc");Q0=makeQuery(id+"F2.boolean.opBoolean","SPLIT",FACE,{"disambiguationData":[TD([makeQuery(id+"F1.opExtrude","SWEPT_FACE",FACE,{"disambiguationData":[OSD([subQ6])]})])],"derivedFrom":makeQuery(id+"F1.opExtrude","CAP_FACE",FACE,{"disambiguationData":[OSD([subQ6,subQ8,subQ9,subQ7,subQ4,subQ3,subQ2,subQ1,subQ0,subQ5,subQ10,subQ11])],"isStart":true})});}
            var sketch = newSketch(context, id + "F16", { "sketchPlane" : qUnion([Q0])});
            skLineSegment(sketch, "E79", {"start": v(0, 90) * mm, "end": v(0, 120) * mm, "construction": true});
            skCircle(sketch, "E80", {"center": v(0, 120) * mm, "radius": 6 * mm});
            skArc(sketch, "E81", {"start": v(15, 120) * mm, "mid": v(0, 135) * mm, "end": v(-15, 120) * mm});
            skLineSegment(sketch, "E82", {"start": v(-33, 90) * mm, "end": v(-15, 108) * mm});
            skLineSegment(sketch, "E83", {"start": v(-15, 108) * mm, "end": v(-15, 120) * mm});
            skLineSegment(sketch, "E84", {"start": v(15, 120) * mm, "end": v(15, 108) * mm});
            skLineSegment(sketch, "E85", {"start": v(15, 108) * mm, "end": v(33, 90) * mm});
            skLineSegment(sketch, "E86", {"start": v(-80, 0) * mm, "end": v(80, 0) * mm, "construction": true});
            skLineSegment(sketch, "E87.MirrorCS", {"start": v(-33, -90) * mm, "end": v(-15, -108) * mm});
            skLineSegment(sketch, "E88.MirrorCS", {"start": v(-15, -108) * mm, "end": v(-15, -120) * mm});
            skArc(sketch, "E89.MirrorCS", {"start": v(15, -120) * mm, "mid": v(0, -135) * mm, "end": v(-15, -120) * mm});
            skCircle(sketch, "E90.MirrorC", {"center": v(0, -120) * mm, "radius": 6 * mm});
            skLineSegment(sketch, "E91.MirrorCS", {"start": v(15, -120) * mm, "end": v(15, -108) * mm});
            skLineSegment(sketch, "E92.MirrorCS", {"start": v(15, -108) * mm, "end": v(33, -90) * mm});
            skSolve(sketch);
        }
        {
            var Q0;
            Q0=makeQuery(id+"F16.imprint","IMPRINT",FACE,{"disambiguationData":[TD([[makeQuery(id+"F16.imprint","IMPRINT",EDGE,{"derivedFrom":sQuery(id+"F16.wireOp",EDGE,"E80")}),-1.0]])]});
            var Q1;
            Q1=makeQuery(id+"F16.imprint","IMPRINT",FACE,{"disambiguationData":[TD([[makeQuery(id+"F16.imprint","IMPRINT",EDGE,{"derivedFrom":makeQuery(id+"F1.opExtrude","CAP_EDGE",EDGE,{"disambiguationData":[OSD([sQuery(id+"F0.wireOp",EDGE,"E1.left")])],"isStart":true})}),-1.0]])]});
            var Q2;
            {var subQ0=sQuery(id+"F16.wireOp",EDGE,"E87.MirrorCS");Q2=makeQuery(id+"F16.imprint","IMPRINT",FACE,{"disambiguationData":[TD([[makeQuery(id+"F16.imprint","IMPRINT",EDGE,{"derivedFrom":subQ0}),1.0]])]});}
            var Q3;
            Q3=makeQuery(id+"F2.opExtrude","CAP_FACE",FACE,{"disambiguationData":[OSD([sQuery(id+"F0.wireOp",EDGE,"E12"),sQuery(id+"F0.wireOp",EDGE,"E13"),sQuery(id+"F0.wireOp",EDGE,"E14"),sQuery(id+"F0.wireOp",EDGE,"E15"),sQuery(id+"F0.wireOp",EDGE,"E17.filletArc"),sQuery(id+"F0.wireOp",EDGE,"E18.filletArc"),sQuery(id+"F0.wireOp",EDGE,"E19.filletArc"),sQuery(id+"F0.wireOp",EDGE,"E20.filletArc"),sQuery(id+"F0.wireOp",EDGE,"E25.0"),sQuery(id+"F0.wireOp",EDGE,"E25.1"),sQuery(id+"F0.wireOp",EDGE,"E25.2"),sQuery(id+"F0.wireOp",EDGE,"E25.3"),sQuery(id+"F0.wireOp",EDGE,"E25.4"),sQuery(id+"F0.wireOp",EDGE,"E25.5"),sQuery(id+"F0.wireOp",EDGE,"E25.6"),sQuery(id+"F0.wireOp",EDGE,"E25.7")])],"isStart":false});
            extrude(context, id + "F17", {"entities" : qUnion([Q0, Q1, Q2]), "endBound" : BoundingType.UP_TO_SURFACE, "depth" : 25 * mm, "endBoundEntityFace" : qUnion([Q3]), "offsetDistance" : 25 * mm});
        }
    });
